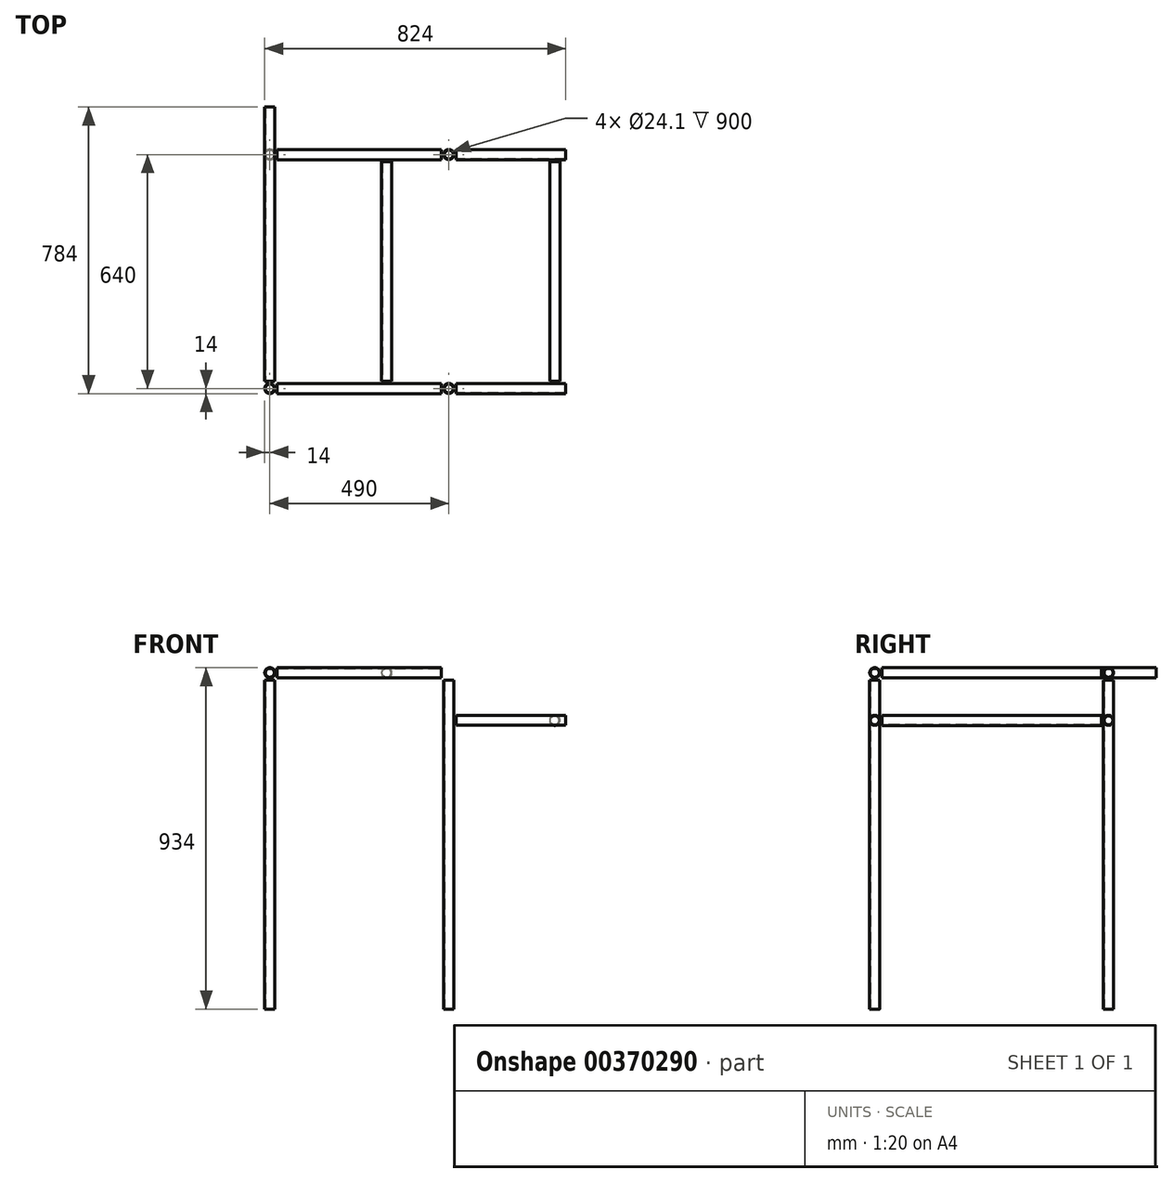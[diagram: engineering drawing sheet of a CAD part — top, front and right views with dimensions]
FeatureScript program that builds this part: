
annotation { "Feature Type Name" : "Feature", "Feature Type Description" : "" }
export const myFeature = defineFeature(function(context is Context, id is Id, definition is map)
    precondition{}
    {
        {
            var Q0;
            Q0=qCreatedBy(makeId("Top.planeOp"),FACE);
            var sketch = newSketch(context, id + "F0", { "sketchPlane" : qUnion([Q0])});
            skCircle(sketch, "E0", {"center": v(0, 0) * mm, "radius": 12.05 * mm});
            skCircle(sketch, "E1", {"center": v(0, 0) * mm, "radius": 14 * mm});
            skCircle(sketch, "E2.0.1.0", {"center": v(0, 640) * mm, "radius": 14 * mm});
            skCircle(sketch, "E2.0.1.1", {"center": v(0, 640) * mm, "radius": 12.05 * mm});
            skCircle(sketch, "E2.1.0.0", {"center": v(-490, 0) * mm, "radius": 14 * mm});
            skCircle(sketch, "E2.1.0.1", {"center": v(-490, 0) * mm, "radius": 12.05 * mm});
            skCircle(sketch, "E2.1.1.0", {"center": v(-490, 640) * mm, "radius": 14 * mm});
            skCircle(sketch, "E2.1.1.1", {"center": v(-490, 640) * mm, "radius": 12.05 * mm});
            skLineSegment(sketch, "E2.direction1", {"start": v(-490, 0) * mm, "end": v(0, 0) * mm, "construction": true});
            skLineSegment(sketch, "E2.direction2", {"start": v(0, 0) * mm, "end": v(0, 640) * mm, "construction": true});
            skSolve(sketch);
        }
        {
            var Q0;
            Q0 = qSketchRegion(id + "F0", true);
            extrude(context, id + "F1", {"entities" : qUnion([Q0]), "depth" : 880 * mm, "hasSecondDirection" : true, "secondDirectionOppositeDirection" : true, "secondDirectionDepth" : 20 * mm});
        }
        {
            var Q0;
            Q0=qCreatedBy(makeId("Front.planeOp"),FACE);
            var sketch = newSketch(context, id + "F2", { "sketchPlane" : qUnion([Q0])});
            skCircle(sketch, "E3", {"center": v(290, 770) * mm, "radius": 12.05 * mm});
            skCircle(sketch, "E4", {"center": v(290, 770) * mm, "radius": 14 * mm});
            skCircle(sketch, "E5", {"center": v(-170, 900) * mm, "radius": 12.05 * mm});
            skCircle(sketch, "E6", {"center": v(-170, 900) * mm, "radius": 14 * mm});
            skCircle(sketch, "E7", {"center": v(-490, 900) * mm, "radius": 12.05 * mm});
            skCircle(sketch, "E8", {"center": v(-490, 900) * mm, "radius": 14 * mm});
            skSolve(sketch);
        }
        {
            var Q0;
            Q0 = qSketchRegion(id + "F2", true);
            extrude(context, id + "F3", {"entities" : qUnion([Q0]), "oppositeDirection" : true, "depth" : 620 * mm, "hasSecondDirection" : true, "secondDirectionOppositeDirection" : true, "secondDirectionDepth" : 20 * mm});
        }
        {
            var Q0;
            Q0=qCreatedBy(makeId("Right.planeOp"),FACE);
            var sketch = newSketch(context, id + "F4", { "sketchPlane" : qUnion([Q0])});
            skCircle(sketch, "E9.1.0.0", {"center": v(0, 900) * mm, "radius": 14 * mm});
            skCircle(sketch, "E9.1.0.1", {"center": v(0, 900) * mm, "radius": 12.05 * mm});
            skCircle(sketch, "E10.1.0.0", {"center": v(640, 900) * mm, "radius": 12.05 * mm});
            skCircle(sketch, "E10.1.0.1", {"center": v(640, 900) * mm, "radius": 14 * mm});
            skLineSegment(sketch, "E10.direction1", {"start": v(0, 900) * mm, "end": v(640, 900) * mm, "construction": true});
            skSolve(sketch);
        }
        {
            var Q0;
            Q0=makeQuery(id+"F4.imprint","IMPRINT",FACE,{"disambiguationData":[TD([[makeQuery(id+"F4.imprint","IMPRINT",EDGE,{"derivedFrom":sQuery(id+"F4.wireOp",EDGE,"E10.1.0.0")}),-1.0]])]});
            var Q1;
            Q1=makeQuery(id+"F4.imprint","IMPRINT",FACE,{"disambiguationData":[TD([[makeQuery(id+"F4.imprint","IMPRINT",EDGE,{"derivedFrom":sQuery(id+"F4.wireOp",EDGE,"E9.1.0.0")}),1.0]])]});
            extrude(context, id + "F5", {"entities" : qUnion([Q0, Q1]), "oppositeDirection" : true, "depth" : 470 * mm, "hasSecondDirection" : true, "secondDirectionOppositeDirection" : true, "secondDirectionDepth" : 20 * mm});
        }
        {
            var Q0;
            Q0=qCreatedBy(makeId("Right.planeOp"),FACE);
            var sketch = newSketch(context, id + "F6", { "sketchPlane" : qUnion([Q0])});
            skCircle(sketch, "E11.0.1.0", {"center": v(0, 770) * mm, "radius": 11.95 * mm});
            skCircle(sketch, "E11.0.1.1", {"center": v(0, 770) * mm, "radius": 13.88 * mm});
            skCircle(sketch, "E11.1.1.0", {"center": v(640, 770) * mm, "radius": 11.95 * mm});
            skCircle(sketch, "E11.1.1.1", {"center": v(640, 770) * mm, "radius": 13.88 * mm});
            skSolve(sketch);
        }
        {
            var Q0;
            Q0 = qSketchRegion(id + "F6", true);
            extrude(context, id + "F7", {"entities" : qUnion([Q0]), "depth" : 320 * mm, "hasSecondDirection" : true, "secondDirectionOppositeDirection" : false, "secondDirectionDepth" : 20 * mm});
        }
        {
            var Q0;
            Q0=makeQuery(id+"F3.opExtrude","CAP_FACE",FACE,{"disambiguationData":[OSD([sQuery(id+"F2.wireOp",EDGE,"E7"),sQuery(id+"F2.wireOp",EDGE,"E8")])],"isStart":false});
            extrude(context, id + "F8", {"entities" : qUnion([Q0]), "operationType" : NewBodyOperationType.ADD, "depth" : 150 * mm});
        }
    });
